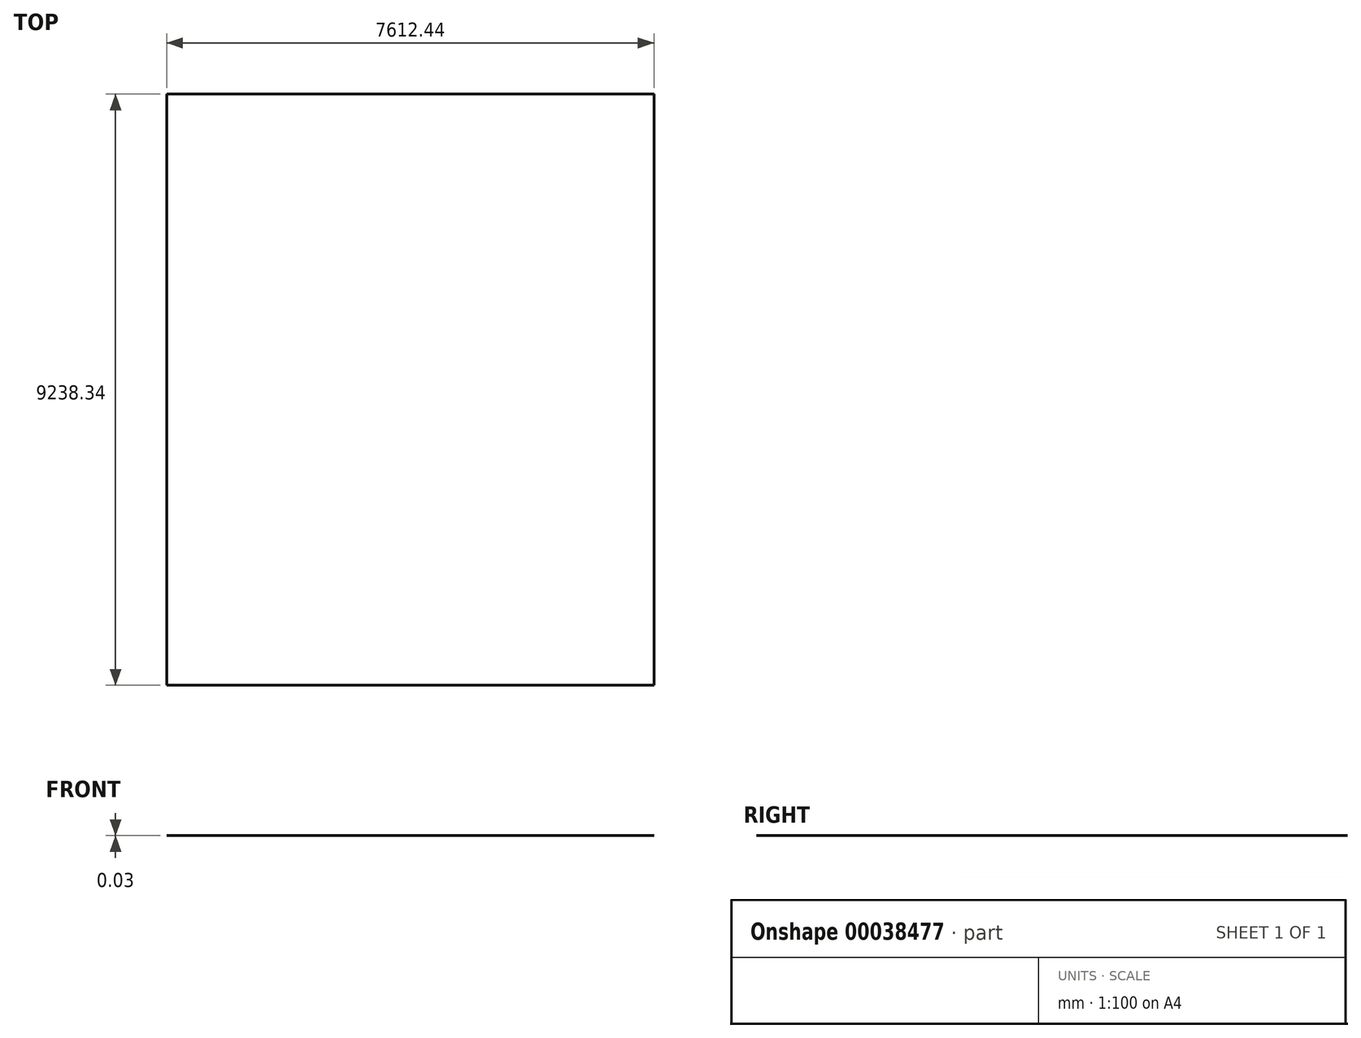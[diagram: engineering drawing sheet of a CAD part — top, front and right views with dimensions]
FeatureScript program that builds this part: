
annotation { "Feature Type Name" : "Feature", "Feature Type Description" : "" }
export const myFeature = defineFeature(function(context is Context, id is Id, definition is map)
    precondition{}
    {
        {
            var Q0;
            Q0=qCreatedBy(makeId("Top.planeOp"),FACE);
            var sketch = newSketch(context, id + "F0", { "sketchPlane" : qUnion([Q0])});
            skLineSegment(sketch, "E0.bottom", {"start": v(-4783.24, 5069.35) * mm, "end": v(2829.2, 5069.35) * mm});
            skLineSegment(sketch, "E0.top", {"start": v(-4783.24, -4169) * mm, "end": v(2829.2, -4169) * mm});
            skLineSegment(sketch, "E0.left", {"start": v(-4783.24, 5069.35) * mm, "end": v(-4783.24, -4169) * mm});
            skLineSegment(sketch, "E0.right", {"start": v(2829.2, 5069.35) * mm, "end": v(2829.2, -4169) * mm});
            skSolve(sketch);
        }
        {
            var Q0;
            Q0=makeQuery(id+"F0.imprint","IMPRINT",FACE,{"disambiguationData":[TD([[makeQuery(id+"F0.imprint","IMPRINT",EDGE,{"derivedFrom":sQuery(id+"F0.wireOp",EDGE,"E0.bottom")}),-1.0]])]});
            extrude(context, id + "F1", {"entities" : qUnion([Q0]), "depth" : 0.03 * mm});
        }
    });
